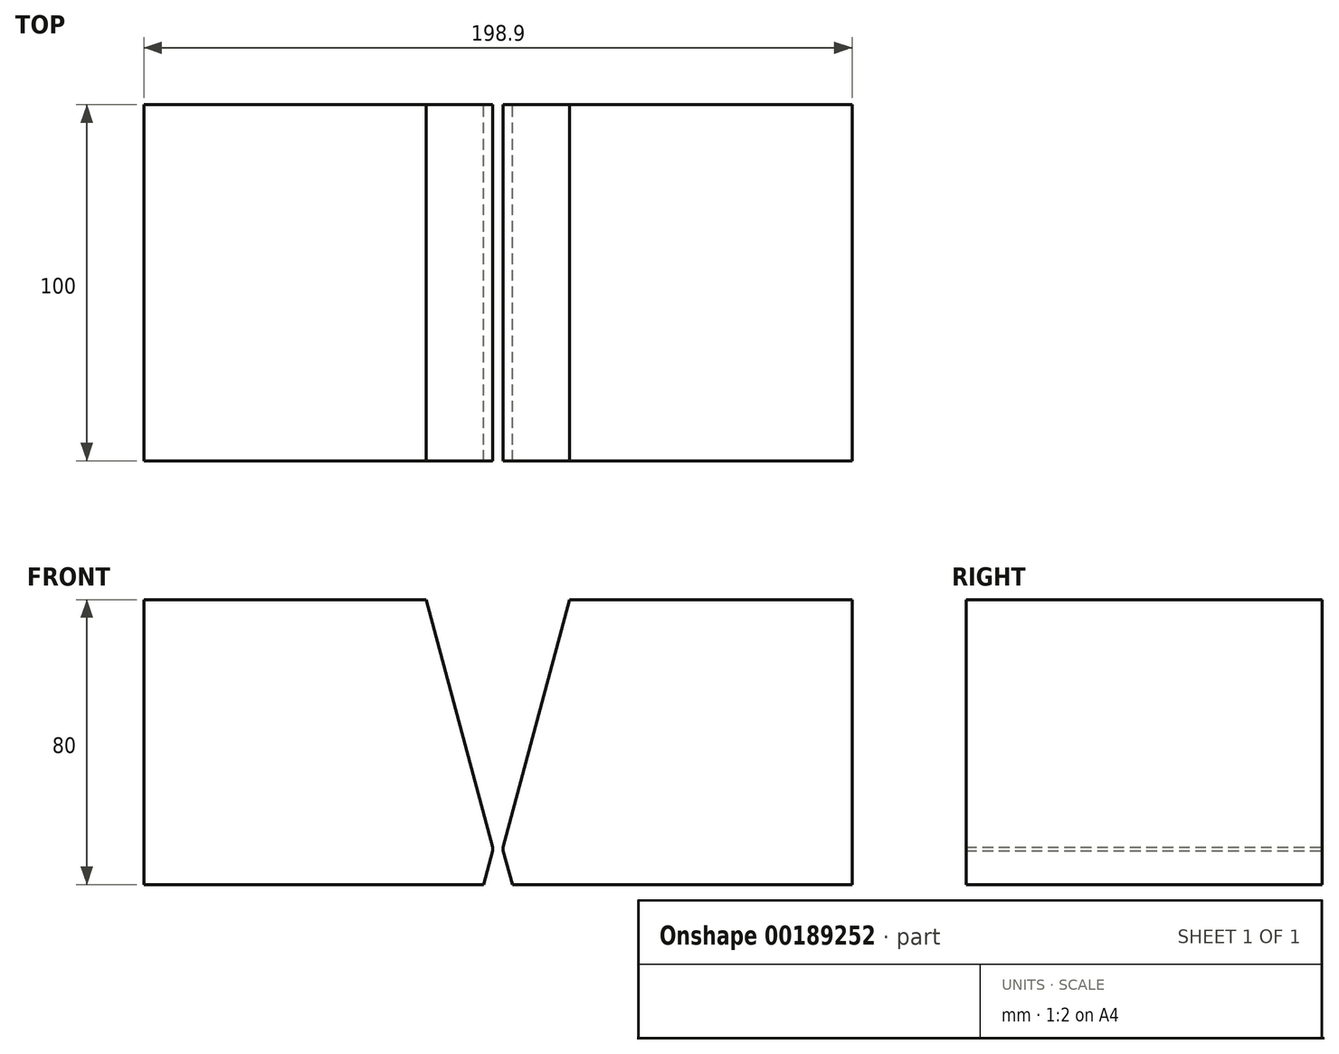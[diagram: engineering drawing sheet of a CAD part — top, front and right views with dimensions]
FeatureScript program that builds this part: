
annotation { "Feature Type Name" : "Feature", "Feature Type Description" : "" }
export const myFeature = defineFeature(function(context is Context, id is Id, definition is map)
    precondition{}
    {
        {
            var Q0;
            Q0=qCreatedBy(makeId("Front.planeOp"),FACE);
            var sketch = newSketch(context, id + "F0", { "sketchPlane" : qUnion([Q0])});
            skLineSegment(sketch, "E0", {"start": v(-34.84, 0) * mm, "end": v(34.9, 0) * mm, "construction": true});
            skLineSegment(sketch, "E1", {"start": v(0, 35.15) * mm, "end": v(0, -34.81) * mm, "construction": true});
            skLineSegment(sketch, "E2", {"start": v(-1.5, 0.5) * mm, "end": v(-20.12, 70) * mm});
            skLineSegment(sketch, "E3", {"start": v(-20.12, 70) * mm, "end": v(-99.45, 70) * mm});
            skLineSegment(sketch, "E4", {"start": v(-99.45, 70) * mm, "end": v(-99.45, -10) * mm});
            skLineSegment(sketch, "E5", {"start": v(-99.45, -10) * mm, "end": v(-4.05, -10) * mm});
            skLineSegment(sketch, "E6", {"start": v(-4.05, -10) * mm, "end": v(-1.5, -0.5) * mm});
            skLineSegment(sketch, "E7.MirrorCS", {"start": v(99.45, 70) * mm, "end": v(99.45, -10) * mm});
            skLineSegment(sketch, "E8.MirrorCS", {"start": v(20.12, 70) * mm, "end": v(99.45, 70) * mm});
            skLineSegment(sketch, "E9.MirrorCS", {"start": v(99.45, -10) * mm, "end": v(4.05, -10) * mm});
            skLineSegment(sketch, "E10.MirrorCS", {"start": v(4.05, -10) * mm, "end": v(1.5, -0.5) * mm});
            skLineSegment(sketch, "E11.MirrorCS", {"start": v(1.5, 0.5) * mm, "end": v(20.12, 70) * mm});
            skLineSegment(sketch, "E12", {"start": v(-1.5, 0.5) * mm, "end": v(-1.5, -0.5) * mm});
            skLineSegment(sketch, "E13", {"start": v(1.5, 0.5) * mm, "end": v(1.5, -0.5) * mm});
            skSolve(sketch);
        }
        {
            var Q0;
            Q0=makeQuery(id+"F0.imprint","IMPRINT",FACE,{"disambiguationData":[TD([[makeQuery(id+"F0.imprint","IMPRINT",EDGE,{"derivedFrom":sQuery(id+"F0.wireOp",EDGE,"E2")}),1.0]])]});
            var Q1;
            Q1=makeQuery(id+"F0.imprint","IMPRINT",FACE,{"disambiguationData":[TD([[makeQuery(id+"F0.imprint","IMPRINT",EDGE,{"derivedFrom":sQuery(id+"F0.wireOp",EDGE,"E7.MirrorCS")}),-1.0]])]});
            extrude(context, id + "F1", {"entities" : qUnion([Q0, Q1]), "depth" : 100 * mm});
        }
    });
